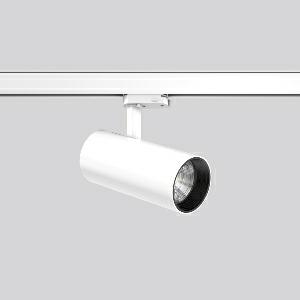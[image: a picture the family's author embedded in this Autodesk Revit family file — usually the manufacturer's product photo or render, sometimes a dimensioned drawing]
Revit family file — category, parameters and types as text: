
# Revit family: deecos_s_mini_742206_002_1_76_43bf
name_source: partatom
category: Lighting Fixtures
units: mm (PartAtom-declared; Revit-internal decimal feet)

## family parameters
Cut with Voids When Loaded = No
Host = Face
Light Source = No
Part Type = Normal
Room Calculation Point = No
Round Connector Dimension = Use Diameter
Shared = No

## types (1)
- DEECOS S mini (1 x LED Modul 940, 3400 lm, 4000)
    Apparent Load = 29 VA
    Approval mark = CE
    CIE Flux Codes = 99 100 100 100 100
    Color Rendering = 92
    Color Temperature = 4000
    Default Elevation = 1800 mm
    Description = Series: DEECOS S mini
LED surface-mounted projector in modern design with no visible cooling ribs. Housing: die-cast aluminium, powder-coated. Rotation range: 356°. Swivel range: 90°. Black plastic ring and recessed LED to prevent glare from the side. Optical assembly with lens made of plastic (polycarbonate) for the best homogeneous light distribution - can be changed without tools. Best colour rendering index Ra>90. With adapter for RZB 3-circuit DALI tracks. Suitable for Track on ceiling, Wall track. High quality converter without flickering and stroboscopic effect. The following accessories can be mounted without use of tools: interchangeable lenses, decorative glasses, honeycomb louvre, clear and frosted diffusers, white interchangeable plastic ring. 
Colour: traffic white, matt (RAL 9016)
Diameter: 87 mm
Height: 214 mm
Lamp: LED
Socket: without socket
Colour temperature: 4000K
Colour rendering index (CRI): 92
System power: 29 W
Rated luminous flux: 3400 lm
Luminous efficiency: 117 lm/W
Control gear: Converter, dimmable, DALI
Protection class: I
Type of protection: IP 20
    Height = 214 mm
    Lamp = 1 x LED Modul 940
    Lamp Light Flux = 3400 lm
    Lamp count = 1
    Length = 87 mm
    Lifetime = 50000 h
    Luminous efficacy = 117 lm/W
    Manufacturer = RZB
    ModVariant = No
    Model = 742206.002.1.76
    Mounting Place = Ceiling
    Mounting Type = Rail mounted
    Number of Poles = 1
    OnlyDefault = Yes
    Power Factor = 1
    Product Name = DEECOS S mini
    Product group = Track mounted projectors
    ProductGroupID = 301
    Protection Class = Protection class I
    Protection Degree = IP 20
    RLX_Detail_Level = 1
    RLX_Emergency_Light_Flux = 0 lm
    RLX_Emergency_Type = 0
    RLX_Emergency_Type_DB = No
    RlxData = <blob elided: 35109 chars, md5=21b84b87>
    Socket = socket
    Standby Power = 0 W
    System Light Flux = 3400 lm
    System Power = 29 W
    Type Comments = Product without accessories
    Type Image = 741930.002.jpg
    URL = http://relux.com
    VarID = ---
    Voltage = 230 V
    Voltage Range = 220-240 V
    Weight = 0.00 kg
    Width = 0 mm  [stored 0 ft]

note: [stored X ft] marks values corroborated as IEEE doubles in the binary element streams (Revit-internal decimal feet)

## geometry (parser evidence)
native form markers: Blend x4, Sweep x12
no freeform markers — native parametric forms only
